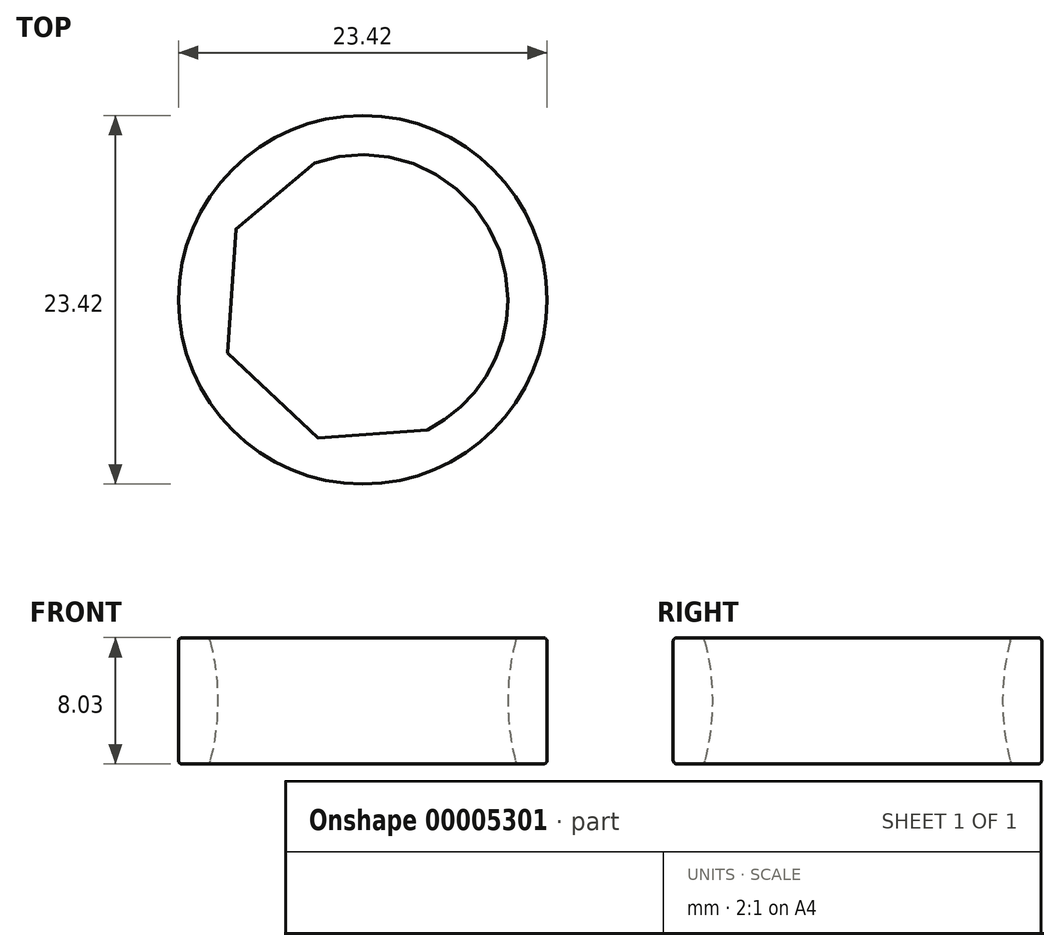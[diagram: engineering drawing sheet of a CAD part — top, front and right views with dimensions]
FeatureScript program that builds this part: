
annotation { "Feature Type Name" : "Feature", "Feature Type Description" : "" }
export const myFeature = defineFeature(function(context is Context, id is Id, definition is map)
    precondition{}
    {
        {
            var Q0;
            Q0=qCreatedBy(makeId("Front.planeOp"),FACE);
            var sketch = newSketch(context, id + "F0", { "sketchPlane" : qUnion([Q0])});
            skLineSegment(sketch, "E0", {"start": v(-9.95, 8.03) * mm, "end": v(-11.46, 8.03) * mm});
            skLineSegment(sketch, "E1", {"start": v(-11.7, 7.77) * mm, "end": v(-11.7, 0.25) * mm});
            skLineSegment(sketch, "E2", {"start": v(-11.46, 0) * mm, "end": v(-9.95, 0) * mm});
            skArc(sketch, "E3", {"start": v(-9.7, 0.2) * mm, "mid": v(-9.22, 4.01) * mm, "end": v(-9.7, 7.84) * mm});
            skPoint(sketch, "E4.visualSharp", {"position": v(-11.7, 0) * mm});
            skArc(sketch, "E4.filletArc", {"start": v(-11.7, 0.25) * mm, "mid": v(-11.64, 0.07) * mm, "end": v(-11.46, 0) * mm});
            skPoint(sketch, "E5.visualSharp", {"position": v(-11.7, 8.03) * mm});
            skArc(sketch, "E5.filletArc", {"start": v(-11.46, 8.03) * mm, "mid": v(-11.64, 7.95) * mm, "end": v(-11.7, 7.77) * mm});
            skPoint(sketch, "E6.visualSharp", {"position": v(-9.75, 8.03) * mm});
            skArc(sketch, "E6.filletArc", {"start": v(-9.7, 7.84) * mm, "mid": v(-9.8, 7.97) * mm, "end": v(-9.95, 8.03) * mm});
            skPoint(sketch, "E7.visualSharp", {"position": v(-9.75, 0) * mm});
            skArc(sketch, "E7.filletArc", {"start": v(-9.95, 0) * mm, "mid": v(-9.8, 0.05) * mm, "end": v(-9.7, 0.2) * mm});
            skLineSegment(sketch, "E8", {"start": v(0, 8.03) * mm, "end": v(0, 0) * mm, "construction": true});
            skSolve(sketch);
        }
        {
            var Q0;
            Q0 = qSketchRegion(id + "F0", true);
            var Q1;
            Q1=sQuery(id+"F0.wireOp",EDGE,"E8");
            revolve(context, id + "F1", {"entities" : qUnion([Q0]), "axis" : qUnion([Q1]), "revolveType" : RevolveType.FULL});
        }
    });
